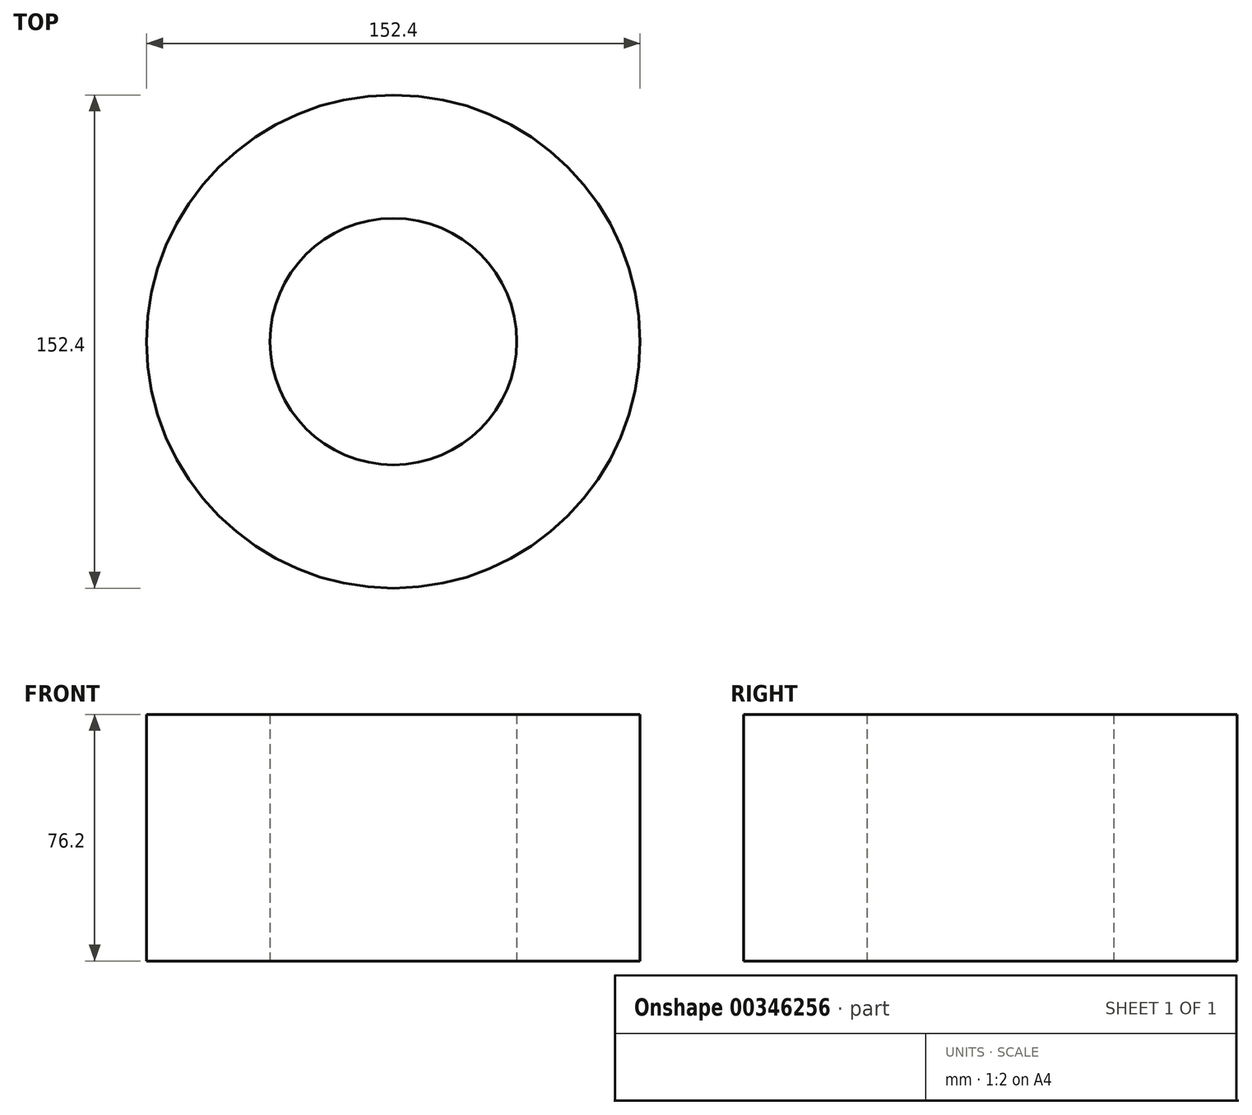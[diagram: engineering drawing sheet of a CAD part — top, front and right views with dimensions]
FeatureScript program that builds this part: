
annotation { "Feature Type Name" : "Feature", "Feature Type Description" : "" }
export const myFeature = defineFeature(function(context is Context, id is Id, definition is map)
    precondition{}
    {
        {
            var Q0;
            Q0=qCreatedBy(makeId("Top.planeOp"),FACE);
            var sketch = newSketch(context, id + "F0", { "sketchPlane" : qUnion([Q0])});
            skCircle(sketch, "E0", {"center": v(0, 0) * mm, "radius": 76.2 * mm});
            skCircle(sketch, "E1", {"center": v(0, 0) * mm, "radius": 38.1 * mm});
            skSolve(sketch);
        }
        {
            var Q0;
            Q0=makeQuery(id+"F0.imprint","IMPRINT",FACE,{"disambiguationData":[TD([[makeQuery(id+"F0.imprint","IMPRINT",EDGE,{"derivedFrom":sQuery(id+"F0.wireOp",EDGE,"E0")}),1.0]])]});
            extrude(context, id + "F1", {"entities" : qUnion([Q0]), "depth" : 76.2 * mm});
        }
    });
